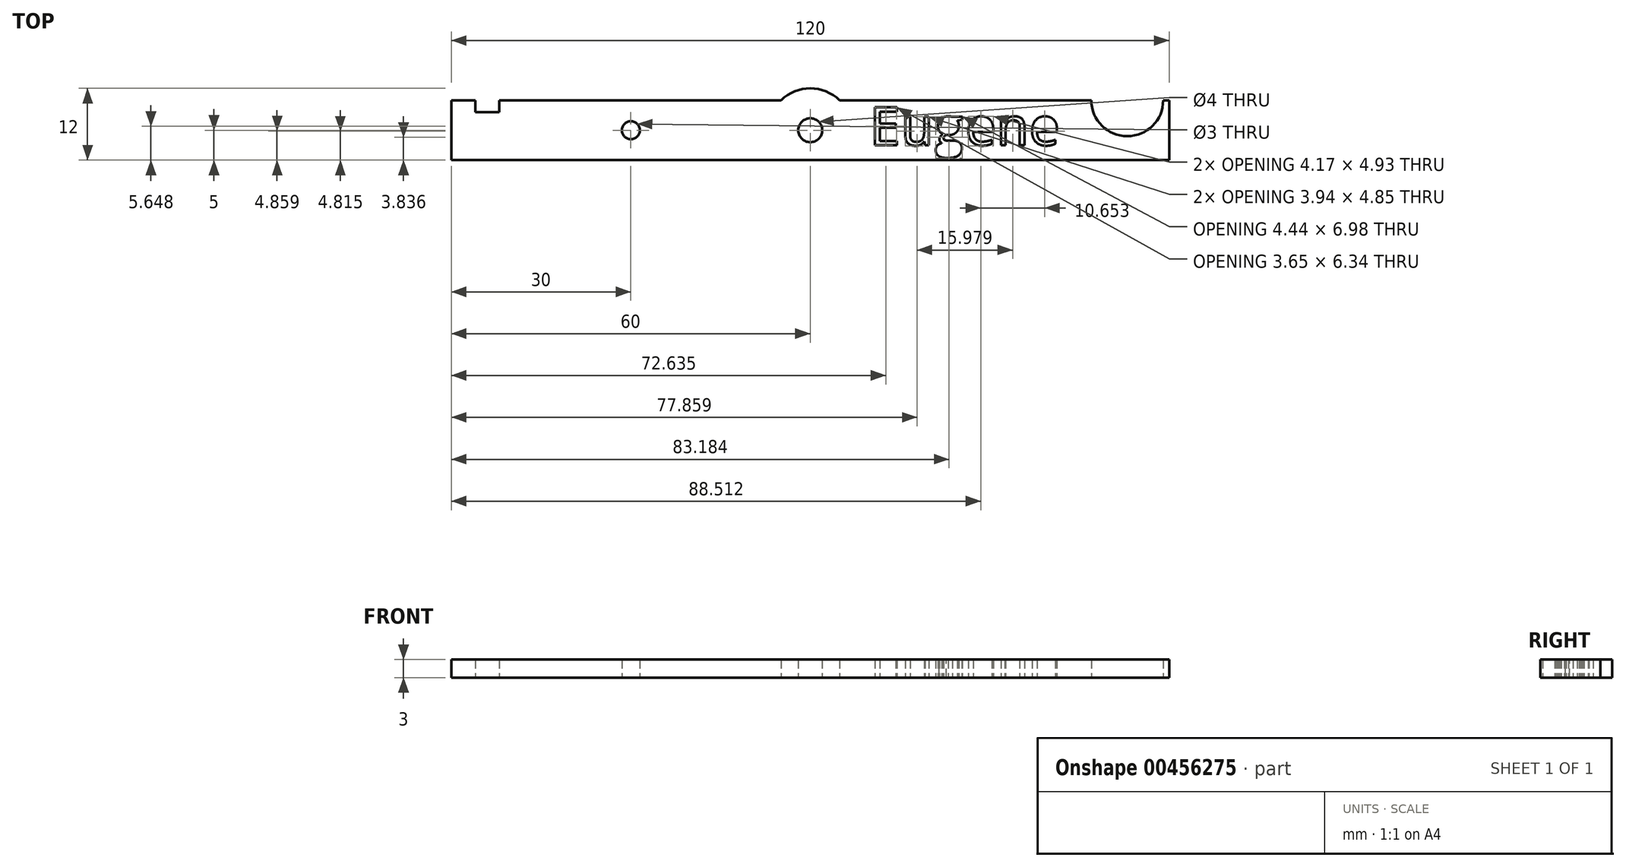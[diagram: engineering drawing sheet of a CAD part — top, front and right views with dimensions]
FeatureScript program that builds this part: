
annotation { "Feature Type Name" : "Feature", "Feature Type Description" : "" }
export const myFeature = defineFeature(function(context is Context, id is Id, definition is map)
    precondition{}
    {
        {
            var Q0;
            Q0=qCreatedBy(makeId("Top.planeOp"),FACE);
            var sketch = newSketch(context, id + "F0", { "sketchPlane" : qUnion([Q0])});
            skLineSegment(sketch, "E0.bottom", {"start": v(-60, 5) * mm, "end": v(60, 5) * mm});
            skLineSegment(sketch, "E0.top", {"start": v(-60, -5) * mm, "end": v(60, -5) * mm});
            skLineSegment(sketch, "E0.left", {"start": v(-60, 5) * mm, "end": v(-60, -5) * mm});
            skLineSegment(sketch, "E0.right", {"start": v(60, 5) * mm, "end": v(60, -5) * mm});
            skPoint(sketch, "E0.middle", {"position": v(0, 0) * mm});
            skLineSegment(sketch, "E1.bottom", {"start": v(-56, 5) * mm, "end": v(-52, 5) * mm});
            skLineSegment(sketch, "E1.top", {"start": v(-56, 3) * mm, "end": v(-52, 3) * mm});
            skLineSegment(sketch, "E1.left", {"start": v(-56, 5) * mm, "end": v(-56, 3) * mm});
            skLineSegment(sketch, "E1.right", {"start": v(-52, 5) * mm, "end": v(-52, 3) * mm});
            skCircle(sketch, "E2", {"center": v(0, 0) * mm, "radius": 2 * mm});
            skCircle(sketch, "E3", {"center": v(0, 0) * mm, "radius": 7 * mm});
            skCircle(sketch, "E4", {"center": v(-30, 0) * mm, "radius": 1.5 * mm});
            skCircle(sketch, "E5", {"center": v(53, 5) * mm, "radius": 6 * mm});
            skText(sketch, "E6", { "text": "Eugene", "fontName": "DroidSansMono.ttf"});
            const initialGuessF0  = {"E6": [0.00987, -0.00252, 1, 0, 0.00639]};
            skSetInitialGuess(sketch, initialGuessF0);
            skSolve(sketch);
        }
        {
            var Q0;
            {var subQ0=sQuery(id+"F0.wireOp",EDGE,"E0.left");Q0=makeQuery(id+"F0.imprint","IMPRINT",FACE,{"disambiguationData":[TD([[makeQuery(id+"F0.imprint","IMPRINT",EDGE,{"derivedFrom":subQ0}),1.0]])]});}
            var Q1;
            Q1=makeQuery(id+"F0.imprint","IMPRINT",FACE,{"disambiguationData":[TD([[makeQuery(id+"F0.imprint","IMPRINT",EDGE,{"derivedFrom":sQuery(id+"F0.wireOp",EDGE,"E2")}),-1.0]])]});
            var Q2;
            {var subQ0=sQuery(id+"F0.wireOp",EDGE,"E3");var subQ1=sQuery(id+"F0.wireOp",EDGE,"E0.top");var subQ2=makeQuery(id+"F0.imprint","INTERSECT",VERTEX,{"disambiguationData":[OD(0.0)],"derivedFrom":[subQ1,subQ0]});Q2=makeQuery(id+"F0.imprint","IMPRINT",FACE,{"disambiguationData":[TD([[makeQuery(id+"F0.imprint","IMPRINT",EDGE,{"disambiguationData":[TD([[subQ2,-1.0]])],"derivedFrom":subQ1}),-1.0]])]});}
            var Q3;
            {var subQ0=sQuery(id+"F0.wireOp",EDGE,"E3");var subQ1=sQuery(id+"F0.wireOp",EDGE,"E0.bottom");var subQ2=makeQuery(id+"F0.imprint","INTERSECT",VERTEX,{"disambiguationData":[OD(0.0)],"derivedFrom":[subQ1,subQ0]});Q3=makeQuery(id+"F0.imprint","IMPRINT",FACE,{"disambiguationData":[TD([[makeQuery(id+"F0.imprint","IMPRINT",EDGE,{"disambiguationData":[TD([[subQ2,-1.0]])],"derivedFrom":subQ1}),1.0]])]});}
            var Q4;
            {var subQ0=sQuery(id+"F0.wireOp",EDGE,"E0.right");Q4=makeQuery(id+"F0.imprint","IMPRINT",FACE,{"disambiguationData":[TD([[makeQuery(id+"F0.imprint","IMPRINT",EDGE,{"derivedFrom":subQ0}),-1.0]])]});}
            extrude(context, id + "F1", {"entities" : qUnion([Q0, Q1, Q2, Q3, Q4]), "depth" : 3 * mm});
        }
    });
